# Revit family: DFM Doors - zweiflügelige Türen EI 120
name_source: partatom
category: Doors
revit_build: Autodesk Revit 2017 (Build: 20190507_1515(x64)
units: mm (PartAtom-declared; Revit-internal decimal feet)

## family parameters
Always vertical = Yes
Cut with Voids When Loaded = No
Host = Wall
OmniClass Number = 23.30.10.00
OmniClass Title = Doors
Room Calculation Point = Yes
Shared = No

## types (1)
- 2018x1840 Innenzarge
    Autor = www.archispace.pl
    Breite zwischen den Zargen = 1851 mm  [stored 6.07283 ft]
    Eckzarge = No
    Fire Rating = EI 120
    Function = Interior
    Gangflügelsbreite = 963.5 mm  [stored 3.16109 ft]
    Height = 2101 mm  [stored 6.89304 ft]
    Innenzarge = Yes
    Manufacturer = DFM Doors sp. z o. o.
    Material des Anschlagprofils = DFM Doors - aluminium
    Material für Wetterschutzschenkel = DFM Doors - verzinktes Stahlblech
    Material für den Beschlag = DFM Doors - aluminium
    Material für den Türflügel = DFM Doors - verzinktes Stahlblech
    Material für den Türschließer = DFM Doors - aluminium
    Material für die Türbänder = DFM Doors - Edelstahl
    Material für die Verglasung = DFM Doors - Verglasung
    Material für die Verglasungsrahmen = DFM Doors - verzinktes Stahlblech
    Material für die Zarge = DFM Doors - verzinktes Stahlblech
    Model = DFM DS 120 - 2
    Rough Height = 2101 mm  [stored 6.89304 ft]
    Rough Width = 2017 mm  [stored 6.61745 ft]
    Standflügelbreite = 963.5 mm  [stored 3.16109 ft]
    Thickness = 65 mm  [stored 0.213255 ft]
    Türflügelhöhe = 2050 mm  [stored 6.72572 ft]
    URL = https://www.dfm-europe.eu
    Versatz der Gangflügelachse = 523.75 mm
    Versatz der Standflügelachse = 523.75 mm
    Versatz der Zwischenflügelachse = 1008.5 mm  [stored 3.30873 ft]
    Versatz des Türflügels = 58 mm  [stored 0.190289 ft]
    Wall Closure = By host
    Wandumfassungszarge = No
    Width = 2017 mm  [stored 6.61745 ft]
    Zarge typ = 2
    lichte Durchgangsbreite = 1840 mm  [stored 6.03675 ft]
    lichte Durchgangsbreite Max./Min. = ok
    lichte Durchgangsbreite bei geöffnetem Gangflügel = 870.5 mm  [stored 2.85597 ft]
    lichte Durchgangshöhe = 2018 mm  [stored 6.62073 ft]
    lichte Durchgangshöhe Max./Min. = ok

note: [stored X ft] marks values corroborated as IEEE doubles in the binary element streams (Revit-internal decimal feet)
